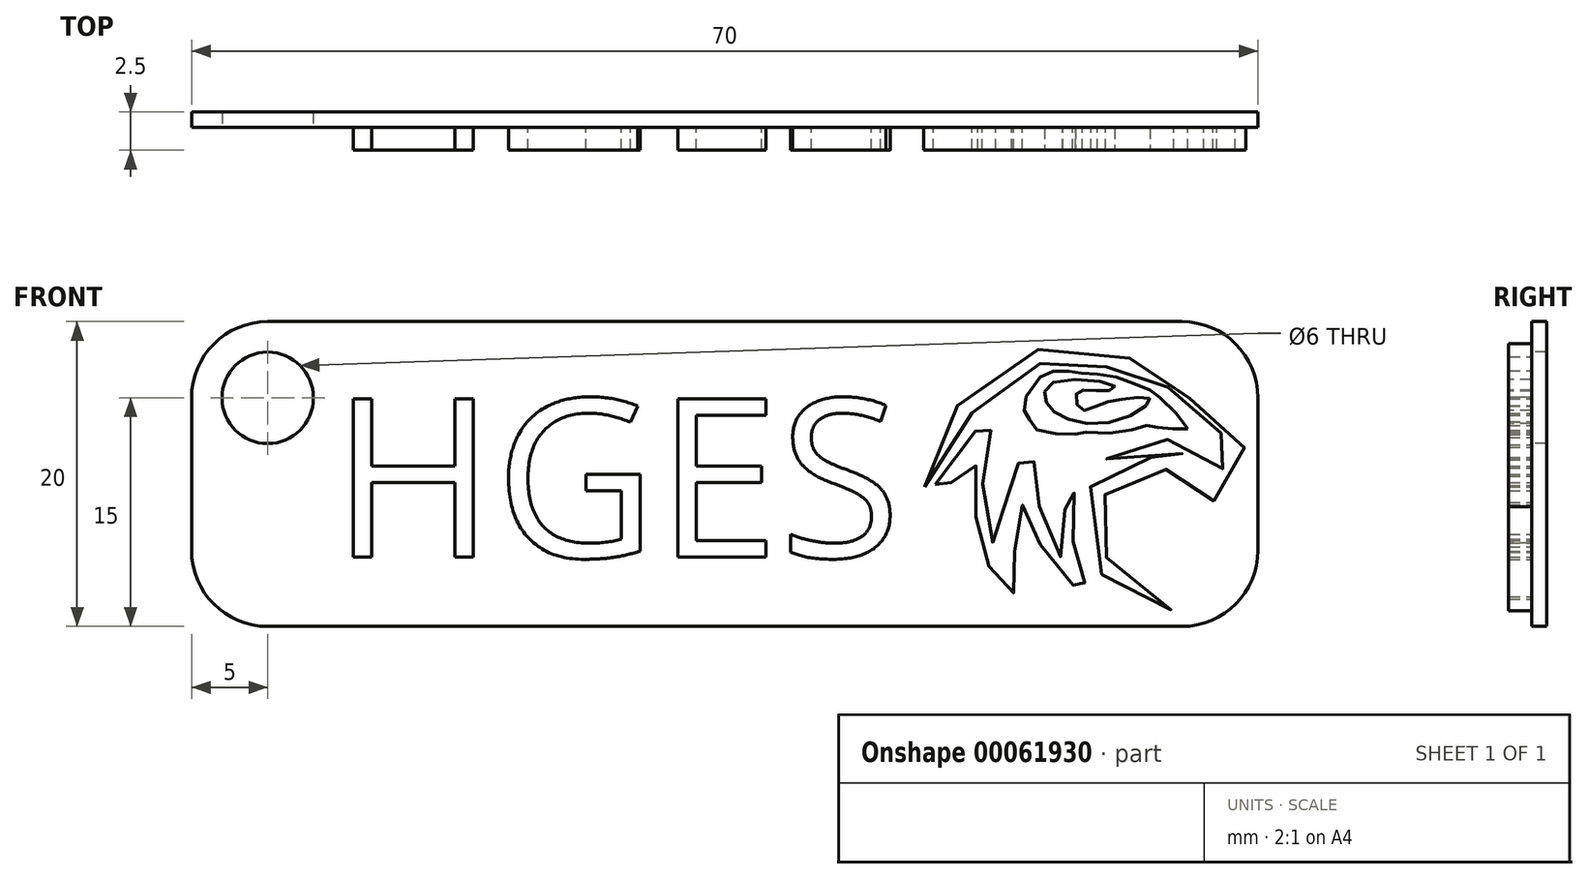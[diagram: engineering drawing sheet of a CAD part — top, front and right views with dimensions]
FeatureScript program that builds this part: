
annotation { "Feature Type Name" : "Feature", "Feature Type Description" : "" }
export const myFeature = defineFeature(function(context is Context, id is Id, definition is map)
    precondition{}
    {
        {
            var Q0;
            Q0=qCreatedBy(makeId("Front.planeOp"),FACE);
            var sketch = newSketch(context, id + "F0", { "sketchPlane" : qUnion([Q0])});
            skLineSegment(sketch, "E0.bottom", {"start": v(-25, 9) * mm, "end": v(45, 9) * mm});
            skLineSegment(sketch, "E0.top", {"start": v(-25, -11) * mm, "end": v(45, -11) * mm});
            skLineSegment(sketch, "E0.left", {"start": v(-25, 9) * mm, "end": v(-25, -11) * mm});
            skLineSegment(sketch, "E0.right", {"start": v(45, 9) * mm, "end": v(45, -11) * mm});
            skSolve(sketch);
        }
        {
            var Q0;
            Q0=makeQuery(id+"F0.imprint","IMPRINT",FACE,{"disambiguationData":[TD([[makeQuery(id+"F0.imprint","IMPRINT",EDGE,{"derivedFrom":sQuery(id+"F0.wireOp",EDGE,"E0.bottom")}),-1.0]])]});
            extrude(context, id + "F1", {"entities" : qUnion([Q0]), "oppositeDirection" : true, "depth" : 1 * mm});
        }
        {
            var Q0;
            Q0=makeQuery(id+"F1.opExtrude","CAP_FACE",FACE,{"disambiguationData":[OSD([sQuery(id+"F0.wireOp",EDGE,"E0.bottom"),sQuery(id+"F0.wireOp",EDGE,"E0.top"),sQuery(id+"F0.wireOp",EDGE,"E0.left"),sQuery(id+"F0.wireOp",EDGE,"E0.right")])],"isStart":true});
            var sketch = newSketch(context, id + "F2", { "sketchPlane" : qUnion([Q0])});
            skCircle(sketch, "E1", {"center": v(-20, 4) * mm, "radius": 3 * mm});
            skSolve(sketch);
        }
        {
            var Q0;
            Q0=makeQuery(id+"F1.opExtrude","CAP_FACE",FACE,{"disambiguationData":[OSD([sQuery(id+"F0.wireOp",EDGE,"E0.bottom"),sQuery(id+"F0.wireOp",EDGE,"E0.top"),sQuery(id+"F0.wireOp",EDGE,"E0.left"),sQuery(id+"F0.wireOp",EDGE,"E0.right")])],"isStart":true});
            var sketch = newSketch(context, id + "F3", { "sketchPlane" : qUnion([Q0])});
            skFitSpline(sketch, "E2", {"points": [v(23.82, -1.68) * mm, v(26, 1.34) * mm, v(27.75, 2.92) * mm, v(27.33, 1.5) * mm, v(26.91, -1) * mm, v(27.24, -3.93) * mm, v(27.75, -5.77) * mm, v(28.08, -4.35) * mm, v(28.67, -1.76) * mm, v(29.42, 0) * mm, v(30.09, 0.92) * mm, v(30.34, -0.92) * mm, v(30.5, -2.43) * mm, v(31.1, -4.52) * mm, v(32.1, -6.44) * mm, v(32.18, -4.27) * mm, v(32.6, -2.43) * mm, v(32.76, -1.76) * mm, v(33.02, -2.93) * mm, v(32.85, -5.02) * mm, v(33.1, -6.61) * mm, v(33.6, -8.12) * mm, v(34.02, -9.2) * mm, v(32.68, -8.12) * mm, v(31.1, -6.28) * mm, v(30.09, -4.18) * mm, v(29.59, -3.01) * mm, v(29.08, -4.6) * mm, v(29, -6.53) * mm, v(28.83, -7.86) * mm, v(28.92, -9.04) * mm, v(27.75, -7.78) * mm, v(26.91, -5.86) * mm, v(26.4, -3.43) * mm, v(26.33, -1) * mm, v(26.58, 0) * mm, v(25.49, -0.76) * mm, v(23.82, -2.85) * mm, v(23.82, -1.68) * mm]});
            skSolve(sketch);
        }
        {
            var Q0;
            Q0=qSketchRegion(id+"F3",true);
            extrude(context, id + "F4", {"entities" : qUnion([Q0]), "operationType" : NewBodyOperationType.ADD, "depth" : 1.5 * mm});
        }
        {
            var Q0;
            Q0=makeQuery(id+"F1.opExtrude","CAP_FACE",FACE,{"disambiguationData":[OSD([sQuery(id+"F0.wireOp",EDGE,"E0.bottom"),sQuery(id+"F0.wireOp",EDGE,"E0.top"),sQuery(id+"F0.wireOp",EDGE,"E0.left"),sQuery(id+"F0.wireOp",EDGE,"E0.right")])],"isStart":true});
            var sketch = newSketch(context, id + "F5", { "sketchPlane" : qUnion([Q0])});
            skFitSpline(sketch, "E3", {"points": [v(23.1, -1.86) * mm, v(23.81, 0.98) * mm, v(25.7, 3.98) * mm, v(28.86, 6.43) * mm, v(33.05, 7.54) * mm, v(36.28, 6.67) * mm, v(39.13, 5.8) * mm, v(40.23, 4.23) * mm, v(41.97, 3.12) * mm, v(43.79, 1.46) * mm, v(43.87, -1.22) * mm, v(42.05, -3.11) * mm, v(42.3, -1.77) * mm, v(40.95, -0.83) * mm, v(38.5, -0.67) * mm, v(37.08, -0.67) * mm, v(35.03, -2.25) * mm, v(34.48, -3.83) * mm, v(34.63, -5.33) * mm, v(36.21, -7.85) * mm, v(39.45, -9.75) * mm, v(37.87, -9.9) * mm, v(35.43, -8.33) * mm, v(33.84, -5.96) * mm, v(33.84, -2.1) * mm, v(35.74, -0.6) * mm, v(37, 0) * mm, v(39.84, 0) * mm, v(41.42, 0) * mm, v(37.54, 0.73) * mm, v(35.86, 0.49) * mm, v(35.02, 0) * mm, v(35.55, 1.01) * mm, v(38.54, 1.31) * mm, v(40.72, 1.1) * mm, v(42.25, 0.55) * mm, v(42.92, -1.14) * mm, v(43.47, 0) * mm, v(42.92, 1.39) * mm, v(40.7, 2.88) * mm, v(39.29, 4.23) * mm, v(38.9, 5.02) * mm, v(37.4, 5.49) * mm, v(35.02, 6.04) * mm, v(33.36, 6.67) * mm, v(31.39, 6.43) * mm, v(28.78, 5.4) * mm, v(26.42, 3.2) * mm, v(25.15, 1.7) * mm, v(23.1, -1.86) * mm]});
            skSolve(sketch);
        }
        {
            var Q0;
            Q0=qSketchRegion(id+"F5",true);
            extrude(context, id + "F6", {"entities" : qUnion([Q0]), "operationType" : NewBodyOperationType.ADD, "depth" : 1.5 * mm});
        }
        {
            var Q0;
            Q0=makeQuery(id+"F1.opExtrude","CAP_FACE",FACE,{"disambiguationData":[OSD([sQuery(id+"F0.wireOp",EDGE,"E0.bottom"),sQuery(id+"F0.wireOp",EDGE,"E0.top"),sQuery(id+"F0.wireOp",EDGE,"E0.left"),sQuery(id+"F0.wireOp",EDGE,"E0.right")])],"isStart":true});
            var sketch = newSketch(context, id + "F7", { "sketchPlane" : qUnion([Q0])});
            skFitSpline(sketch, "E4", {"points": [v(40.38, 1.97) * mm, v(39.15, 2.02) * mm, v(38.25, 2.1) * mm, v(37.59, 2.18) * mm, v(36.1, 1.73) * mm, v(33.5, 1.73) * mm, v(33.02, 1.62) * mm, v(30.99, 1.76) * mm, v(30.09, 2.27) * mm, v(29.85, 3.01) * mm, v(29.55, 3.3) * mm, v(30.65, 5.3) * mm, v(31.58, 5.76) * mm, v(32.78, 5.73) * mm, v(33.6, 5.6) * mm, v(35.16, 5.48) * mm, v(36.97, 4.9) * mm, v(38.12, 4.4) * mm, v(38.8, 3.78) * mm, v(40.38, 1.97) * mm]});
            skSolve(sketch);
        }
        {
            var Q0;
            Q0=qSketchRegion(id+"F7",true);
            extrude(context, id + "F8", {"entities" : qUnion([Q0]), "operationType" : NewBodyOperationType.ADD, "depth" : 1.5 * mm});
        }
        {
            var Q0;
            Q0=makeQuery(id+"F8.opExtrude","CAP_FACE",FACE,{"disambiguationData":[OSD([sQuery(id+"F7.wireOp",EDGE,"E4")])],"isStart":false});
            var sketch = newSketch(context, id + "F9", { "sketchPlane" : qUnion([Q0])});
            skFitSpline(sketch, "E5", {"points": [v(35.25, 4.48) * mm, v(35.59, 4.78) * mm, v(31.53, 5) * mm, v(31.03, 3.93) * mm, v(32.06, 2.8) * mm, v(35.8, 2.52) * mm, v(37.92, 3.91) * mm, v(36.47, 3.96) * mm, v(34.55, 3.53) * mm, v(33.38, 3.22) * mm, v(33.05, 4.2) * mm, v(33.58, 4.5) * mm, v(35.25, 4.48) * mm]});
            skSolve(sketch);
        }
        {
            var Q0;
            Q0=qSketchRegion(id+"F9",true);
            extrude(context, id + "F10", {"entities" : qUnion([Q0]), "operationType" : NewBodyOperationType.REMOVE, "oppositeDirection" : true, "depth" : 1.5 * mm});
        }
        {
            var Q0;
            Q0=makeQuery(id+"F1.opExtrude","SWEPT_EDGE",EDGE,{"disambiguationData":[OSD([sQuery(id+"F0.wireOp",EDGE,"E0.bottom"),sQuery(id+"F0.wireOp",EDGE,"E0.left")])]});
            var Q1;
            Q1=makeQuery(id+"F1.opExtrude","SWEPT_EDGE",EDGE,{"disambiguationData":[OSD([sQuery(id+"F0.wireOp",EDGE,"E0.top"),sQuery(id+"F0.wireOp",EDGE,"E0.right")])]});
            var Q2;
            Q2=makeQuery(id+"F1.opExtrude","SWEPT_EDGE",EDGE,{"disambiguationData":[OSD([sQuery(id+"F0.wireOp",EDGE,"E0.bottom"),sQuery(id+"F0.wireOp",EDGE,"E0.right")])]});
            var Q3;
            Q3=makeQuery(id+"F1.opExtrude","SWEPT_EDGE",EDGE,{"disambiguationData":[OSD([sQuery(id+"F0.wireOp",EDGE,"E0.top"),sQuery(id+"F0.wireOp",EDGE,"E0.left")])]});
            fillet(context, id + "F11", {"entities" : qUnion([Q0, Q1, Q2, Q3]), "radius" : 5 * mm, "tangentPropagation" : true, "allowEdgeOverflow" : false});
        }
        {
            var Q0;
            Q0=makeQuery(id+"F1.opExtrude","CAP_FACE",FACE,{"disambiguationData":[OSD([sQuery(id+"F0.wireOp",EDGE,"E0.bottom"),sQuery(id+"F0.wireOp",EDGE,"E0.top"),sQuery(id+"F0.wireOp",EDGE,"E0.left"),sQuery(id+"F0.wireOp",EDGE,"E0.right")])],"isStart":true});
            var sketch = newSketch(context, id + "F12", { "sketchPlane" : qUnion([Q0])});
            skText(sketch, "E6", { "text": "HGES", "fontName": "OpenSans-Regular.ttf"});
            const initialGuessF12  = {"E6": [-0.0158, -0.00645, 1, 0, 0.01046]};
            skSetInitialGuess(sketch, initialGuessF12);
            skSolve(sketch);
        }
        {
            var Q0;
            Q0=qSketchRegion(id+"F12",true);
            extrude(context, id + "F13", {"entities" : qUnion([Q0]), "operationType" : NewBodyOperationType.ADD, "depth" : 1.5 * mm});
        }
        {
            var Q0;
            Q0 = qSketchRegion(id + "F2", true);
            var Q1;
            Q1=makeQuery(id+"F1.opExtrude","CAP_FACE",FACE,{"disambiguationData":[OSD([sQuery(id+"F0.wireOp",EDGE,"E0.bottom"),sQuery(id+"F0.wireOp",EDGE,"E0.top"),sQuery(id+"F0.wireOp",EDGE,"E0.left"),sQuery(id+"F0.wireOp",EDGE,"E0.right")])],"isStart":false});
            extrude(context, id + "F14", {"entities" : qUnion([Q0]), "operationType" : NewBodyOperationType.REMOVE, "endBound" : BoundingType.UP_TO_SURFACE, "oppositeDirection" : true, "endBoundEntityFace" : qUnion([Q1]), "depth" : 25 * mm});
        }
    });
